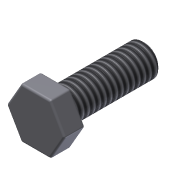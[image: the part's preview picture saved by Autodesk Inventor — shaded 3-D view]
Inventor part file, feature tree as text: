
AUTODESK INVENTOR PART (.ipt)
format: ipt  version: 2011 (Build 150239000, 239)  size: 129,536 bytes
history: native  units: in
note: dims shown in document units (in); Inventor stores cm internally (conversion verified against a paired STEP export)
features: extrude x2, sketch x2, thread x1, chamfer x1, fillet x1
ambient origin geometry x8: Origin, YZ Plane, XZ Plane, XY Plane, X Axis, Y Axis, Z Axis, Center Point
bodies: Solid1 (feature_tree)
feature tree (7):
  extrude  "Extrusion1"  Depth=0.875in TaperAngle=0.0deg
  extrude  "Extrusion2"  Depth=0.2031in TaperAngle=0.0deg
  thread  "Thread1"  [1 undecoded]
  chamfer  "Chamfer1"  Distance=0.02in Angle=45.0deg
  fillet  "Fillet1"  Radius=0.02in
  sketch  "Sketch1"  dims[d0=0.3125in d1=0.875in d2=0.0in]
  sketch  "Sketch2"  dims[d3=0.5in d4=0.2031in d5=0.0in d6=1.0in d7=0.0in d8=0.02in d9=0.125in d10=45.0deg d11=0.02in]
note: 1 required parameter value undecoded (feature->parameter linkage not recoverable at this tier; creation-order binding heuristic only, values carry confidence <= 0.55)
